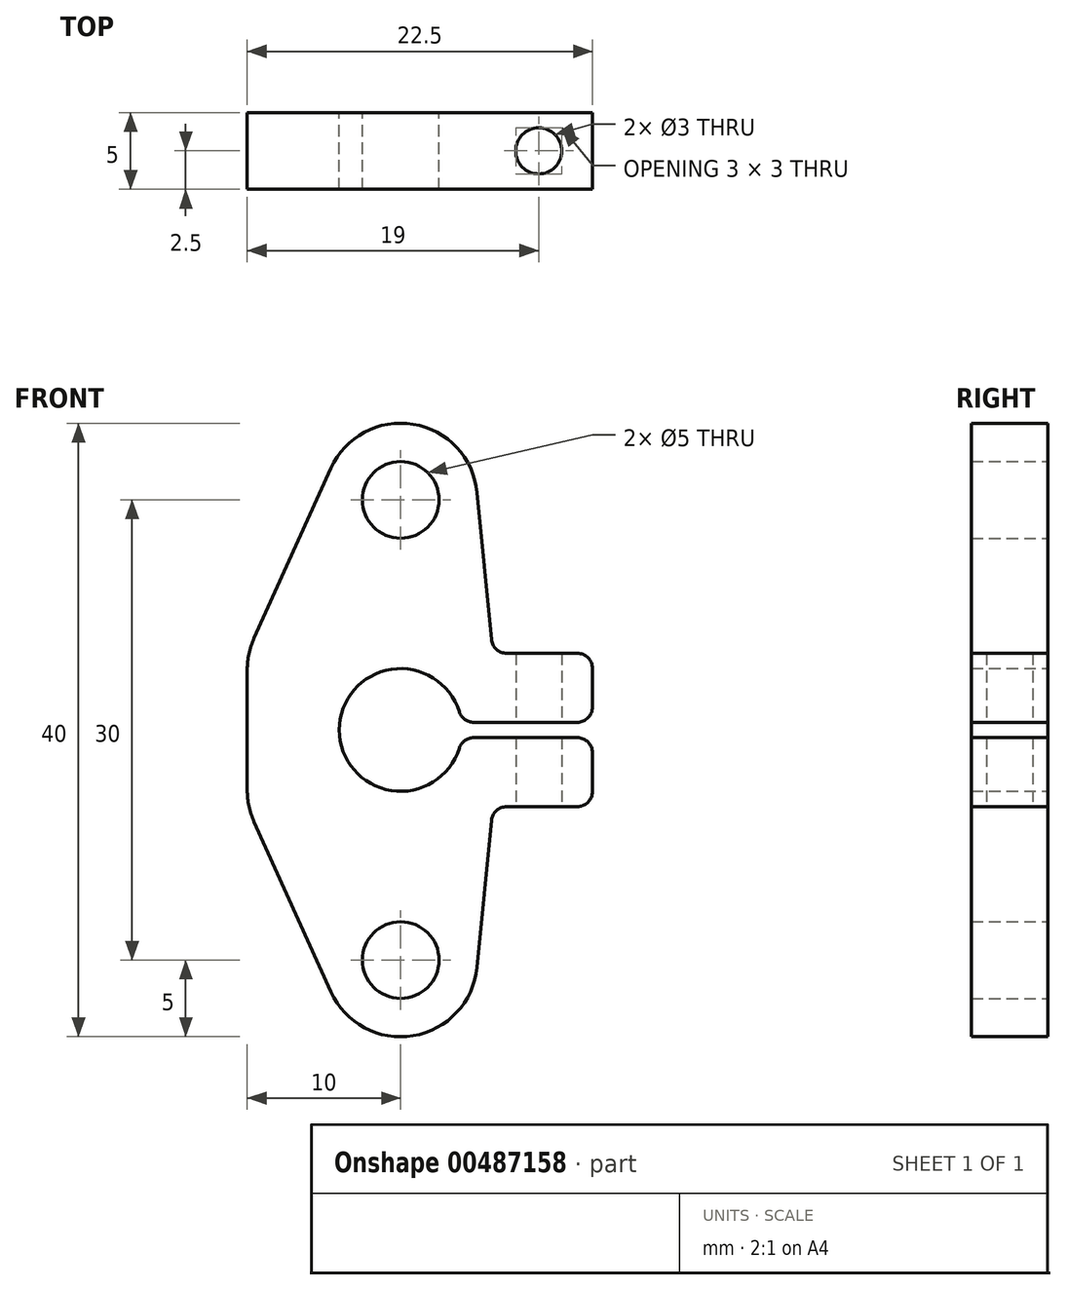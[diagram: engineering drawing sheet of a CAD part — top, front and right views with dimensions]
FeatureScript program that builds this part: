
annotation { "Feature Type Name" : "Feature", "Feature Type Description" : "" }
export const myFeature = defineFeature(function(context is Context, id is Id, definition is map)
    precondition{}
    {
        {
            var Q0;
            Q0=qCreatedBy(makeId("Front.planeOp"),FACE);
            var sketch = newSketch(context, id + "F0", { "sketchPlane" : qUnion([Q0])});
            skArc(sketch, "E0", {"start": v(3.97, 0.5) * mm, "mid": v(-4, 0) * mm, "end": v(3.97, -0.5) * mm});
            skCircle(sketch, "E1", {"center": v(0, 15) * mm, "radius": 2.5 * mm});
            skCircle(sketch, "E2", {"center": v(0, -15) * mm, "radius": 2.5 * mm});
            skArc(sketch, "E3", {"start": v(4.98, 15.49) * mm, "mid": v(0.81, 19.93) * mm, "end": v(-4.56, 17.06) * mm});
            skArc(sketch, "E4", {"start": v(-4.56, -17.06) * mm, "mid": v(0.81, -19.93) * mm, "end": v(4.98, -15.49) * mm});
            skLineSegment(sketch, "E5", {"start": v(-10, 5) * mm, "end": v(-10, -5) * mm});
            skLineSegment(sketch, "E6", {"start": v(-4.56, -17.06) * mm, "end": v(-10, -5) * mm});
            skLineSegment(sketch, "E7", {"start": v(-10, 5) * mm, "end": v(-4.56, 17.06) * mm});
            skLineSegment(sketch, "E8", {"start": v(4.98, -15.49) * mm, "end": v(6, -5) * mm});
            skLineSegment(sketch, "E9", {"start": v(6, -5) * mm, "end": v(12.5, -5) * mm});
            skLineSegment(sketch, "E10", {"start": v(12.5, -5) * mm, "end": v(12.5, -0.5) * mm});
            skLineSegment(sketch, "E11", {"start": v(12.5, 5) * mm, "end": v(6, 5) * mm});
            skLineSegment(sketch, "E12", {"start": v(6, 5) * mm, "end": v(4.98, 15.49) * mm});
            skLineSegment(sketch, "E13", {"start": v(3.97, 0.5) * mm, "end": v(12.5, 0.5) * mm});
            skLineSegment(sketch, "E14", {"start": v(3.97, -0.5) * mm, "end": v(12.5, -0.5) * mm});
            skLineSegment(sketch, "E15.trimOffspring", {"start": v(12.5, 0.5) * mm, "end": v(12.5, 5) * mm});
            skSolve(sketch);
        }
        {
            var Q0;
            Q0=makeQuery(id+"F0.imprint","IMPRINT",FACE,{"disambiguationData":[TD([[makeQuery(id+"F0.imprint","IMPRINT",EDGE,{"derivedFrom":sQuery(id+"F0.wireOp",EDGE,"E0")}),-1.0]])]});
            extrude(context, id + "F1", {"entities" : qUnion([Q0]), "depth" : 5 * mm});
        }
        {
            var Q0;
            Q0=makeQuery(id+"F1.opExtrude","SWEPT_EDGE",EDGE,{"disambiguationData":[OSD([sQuery(id+"F0.wireOp",EDGE,"E5"),sQuery(id+"F0.wireOp",EDGE,"E6")])]});
            var Q1;
            Q1=makeQuery(id+"F1.opExtrude","SWEPT_EDGE",EDGE,{"disambiguationData":[OSD([sQuery(id+"F0.wireOp",EDGE,"E5"),sQuery(id+"F0.wireOp",EDGE,"E7")])]});
            fillet(context, id + "F2", {"entities" : qUnion([Q0, Q1]), "radius" : 5 * mm, "tangentPropagation" : true, "allowEdgeOverflow" : false});
        }
        {
            var Q0;
            Q0=makeQuery(id+"F1.opExtrude","SWEPT_FACE",FACE,{"disambiguationData":[OSD([sQuery(id+"F0.wireOp",EDGE,"E9")])]});
            var sketch = newSketch(context, id + "F3", { "sketchPlane" : qUnion([Q0])});
            skCircle(sketch, "E16", {"center": v(9, 2.5) * mm, "radius": 1.5 * mm});
            skSolve(sketch);
        }
        {
            var Q0;
            Q0 = qSketchRegion(id + "F3", true);
            extrude(context, id + "F4", {"entities" : qUnion([Q0]), "operationType" : NewBodyOperationType.REMOVE, "oppositeDirection" : true, "depth" : 25 * mm});
        }
        {
            var Q0;
            Q0=makeQuery(id+"F1.opExtrude","SWEPT_EDGE",EDGE,{"disambiguationData":[OSD([sQuery(id+"F0.wireOp",EDGE,"E8"),sQuery(id+"F0.wireOp",EDGE,"E9")])]});
            var Q1;
            Q1=makeQuery(id+"F1.opExtrude","SWEPT_EDGE",EDGE,{"disambiguationData":[OSD([sQuery(id+"F0.wireOp",EDGE,"E9"),sQuery(id+"F0.wireOp",EDGE,"E10")])]});
            var Q2;
            Q2=makeQuery(id+"F1.opExtrude","SWEPT_EDGE",EDGE,{"disambiguationData":[OSD([sQuery(id+"F0.wireOp",EDGE,"E11"),sQuery(id+"F0.wireOp",EDGE,"E15.trimOffspring")])]});
            var Q3;
            Q3=makeQuery(id+"F1.opExtrude","SWEPT_EDGE",EDGE,{"disambiguationData":[OSD([sQuery(id+"F0.wireOp",EDGE,"E11"),sQuery(id+"F0.wireOp",EDGE,"E12")])]});
            var Q4;
            Q4=makeQuery(id+"F1.opExtrude","SWEPT_EDGE",EDGE,{"disambiguationData":[OSD([sQuery(id+"F0.wireOp",EDGE,"E13"),sQuery(id+"F0.wireOp",EDGE,"E15.trimOffspring")])]});
            var Q5;
            Q5=makeQuery(id+"F1.opExtrude","SWEPT_EDGE",EDGE,{"disambiguationData":[OSD([sQuery(id+"F0.wireOp",EDGE,"E10"),sQuery(id+"F0.wireOp",EDGE,"E14")])]});
            var Q6;
            Q6=makeQuery(id+"F1.opExtrude","SWEPT_EDGE",EDGE,{"disambiguationData":[OSD([sQuery(id+"F0.wireOp",EDGE,"E0"),sQuery(id+"F0.wireOp",EDGE,"E14")])]});
            var Q7;
            Q7=makeQuery(id+"F1.opExtrude","SWEPT_EDGE",EDGE,{"disambiguationData":[OSD([sQuery(id+"F0.wireOp",EDGE,"E0"),sQuery(id+"F0.wireOp",EDGE,"E13")])]});
            fillet(context, id + "F5", {"entities" : qUnion([Q0, Q1, Q2, Q3, Q4, Q5, Q6, Q7]), "radius" : 1 * mm, "tangentPropagation" : true, "allowEdgeOverflow" : false});
        }
    });
